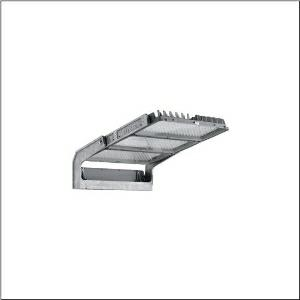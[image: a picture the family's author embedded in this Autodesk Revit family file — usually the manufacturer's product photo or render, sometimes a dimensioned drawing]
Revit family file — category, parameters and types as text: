
# Revit family: floodlight_fl_11_maxi_pro___rs08_5xa779128l02fb_6b31
name_source: partatom
category: Lighting Fixtures
units: mm (PartAtom-declared; Revit-internal decimal feet)

## family parameters
Cut with Voids When Loaded = No
Host = Face
Light Source = No
Part Type = Normal
Room Calculation Point = No
Round Connector Dimension = Use Diameter
Shared = No

## types (1)
- --- (1 x LED, 155960 lm, 1368.3 W, 5700K)
    Apparent Load = 1368 VA
    CIE Flux Codes = 70 87 98 100 100
    Color Rendering = 80
    Color Temperature = 5700K
    Default Elevation = 1800 mm
    Description = Floodlight FL 11  maxi  pro floodlight; light control with lens of PMMA; cover panel of toughened safety glass, transparent; light distribution: RS08, rotationally symmetric direct distribution, LEDcolour temperature: 5700K, rated luminous flux: 155.960lm, colour rendering: CRI > 80, light colour: 857; luminous efficacy: 114lm/W; brightness control: DALI 2; with terminal, 5-pole, max. 2.5mm², mains connection: 220..240V/380..400V AC, 50/60Hz, surge voltage resistance: line to ground: 10kV, service life up to 100,000h L90. Typical operating time: 1000h per year, ECG replaceable separately, LED unit replaceable without ESD environment, dustproof LED module, dimming range 10..100%; 1368W floodlight with 3x LED unit of diecast aluminium, coated grey; length: 1.003mm / width: 651mm / height: 338mm; mounting bracket, of diecast aluminium, uncoated, natural, protection rating (complete): IP66; insulation class (complete): insulation class I (protective earthing); certification: CE, ENEC, VDE; ball protection: ball impact resistant, only for outdoor installations in the designated locations, permissible operating ambient temperature: -45..+55°C, permissible storage temperature: -40..+85°Cpackaging unit: 1 piece

Light Distribution: RS08
    Height = 320 mm
    Lamp = 1 x LED
    Lamp Light Flux = 155960 lm
    Lamp Power = 1368.3 W
    Lamp count = 1
    Length = 1002 mm
    Luminous efficacy = 114 lm/W
    Manufacturer = Siteco
    ModVariant = No
    Model = 5XA779128L02FB
    Mounting Place = Ceiling
    Mounting Type = Surface mounted
    Number of Poles = 1
    OnlyDefault = Yes
    Power Factor = 1
    Product Name = Floodlight FL 11 maxi pro | RS08
    Product group = floodlight | ceiling mounted
    ProductGroupID = 301
    Protection Class = Protection class I
    Protection Degree = IP 66
    RLX_Detail_Level = 1
    RLX_Emergency_Light_Flux = 0 lm
    RLX_Emergency_Type = 0
    RLX_Emergency_Type_DB = No
    RlxData = <blob elided: 40253 chars, md5=5891ba73>
    Socket = socket
    Standby Power = 0 W
    System Light Flux = 155960 lm
    System Power = 1368 W
    Type Comments = factory setting: luminous flux: 100 % | dim-lin: 254 | 935 mA
    Type Image = l_1356210.jpg
    URL = http://relux.com
    VarID = @adj_024634
    Voltage = 0 V
    Weight = 0.00 kg
    Width = 655 mm

## geometry (parser evidence)
native form markers: Blend x4, Sweep x16
no freeform markers — native parametric forms only
